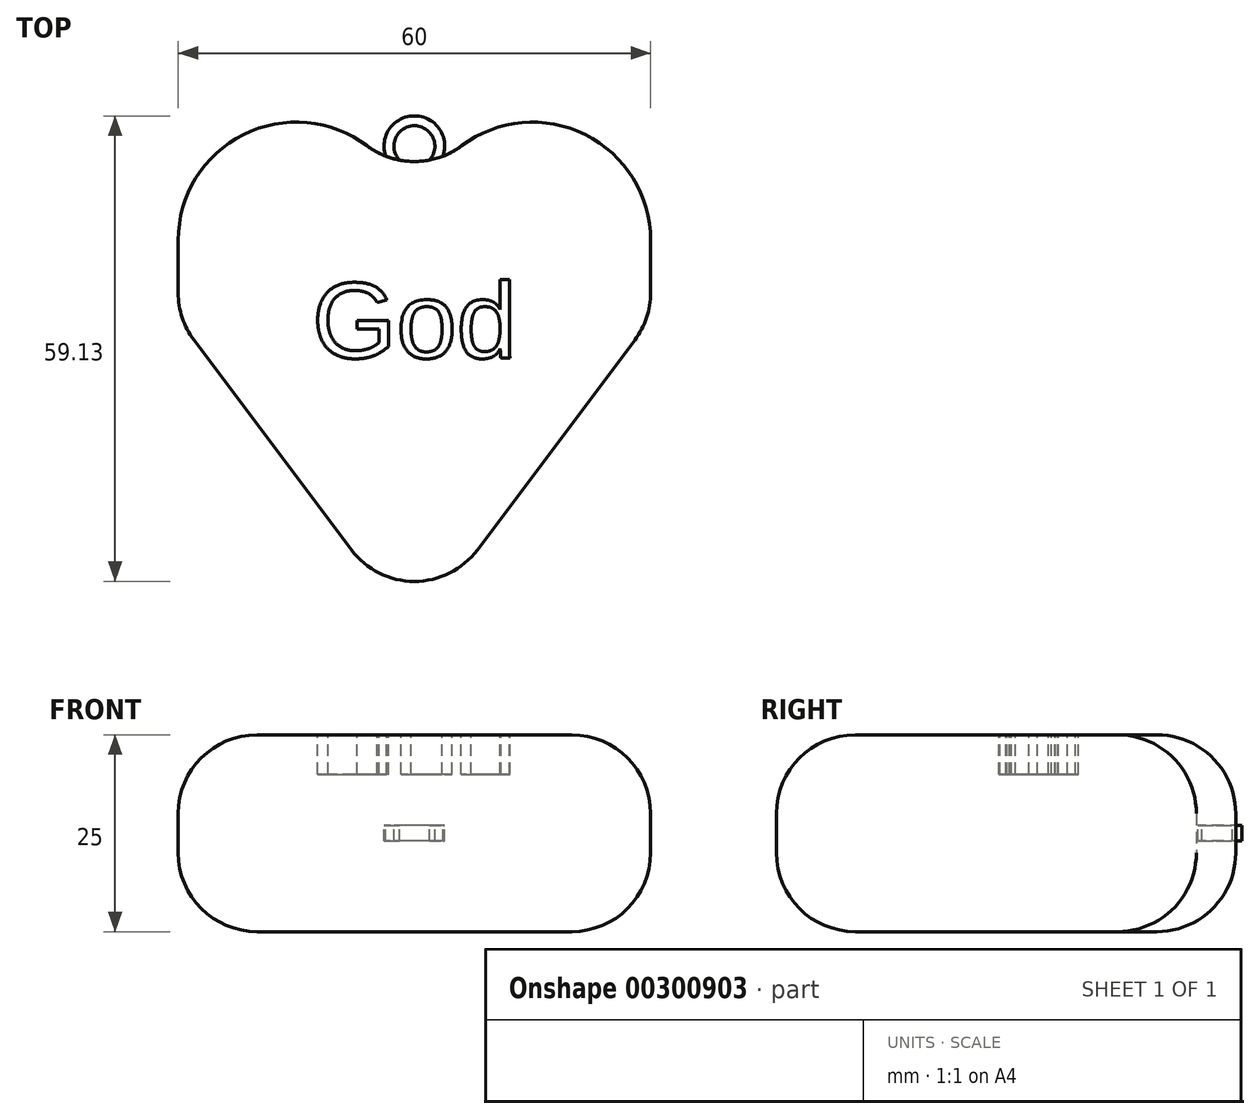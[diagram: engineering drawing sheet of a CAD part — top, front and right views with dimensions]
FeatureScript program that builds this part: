
annotation { "Feature Type Name" : "Feature", "Feature Type Description" : "" }
export const myFeature = defineFeature(function(context is Context, id is Id, definition is map)
    precondition{}
    {
        {
            var Q0;
            Q0=qCreatedBy(makeId("Top.planeOp"),FACE);
            var sketch = newSketch(context, id + "F0", { "sketchPlane" : qUnion([Q0])});
            skLineSegment(sketch, "E0", {"start": v(-30, 0) * mm, "end": v(0, -40) * mm});
            skLineSegment(sketch, "E1", {"start": v(-30, 10) * mm, "end": v(-30, 0) * mm});
            skLineSegment(sketch, "E2", {"start": v(0, 10) * mm, "end": v(0, 0) * mm});
            skArc(sketch, "E3", {"start": v(-30, 10) * mm, "mid": v(-15, 25) * mm, "end": v(0, 10) * mm});
            skArc(sketch, "E4.MirrorCS", {"start": v(30, 10) * mm, "mid": v(15, 25) * mm, "end": v(0, 10) * mm});
            skLineSegment(sketch, "E5.MirrorCS", {"start": v(30, 10) * mm, "end": v(30, 0) * mm});
            skLineSegment(sketch, "E6.MirrorCS", {"start": v(30, 0) * mm, "end": v(0, -40) * mm});
            skSolve(sketch);
        }
        {
            var Q0;
            Q0 = qSketchRegion(id + "F0", true);
            extrude(context, id + "F1", {"entities" : qUnion([Q0]), "endBound" : BoundingType.SYMMETRIC, "oppositeDirection" : true, "depth" : 25 * mm});
        }
        {
            var Q0;
            Q0=makeQuery(id+"F1.opExtrude","CAP_EDGE",EDGE,{"disambiguationData":[OSD([sQuery(id+"F0.wireOp",EDGE,"E5.MirrorCS")])],"isStart":false});
            var Q1;
            Q1=makeQuery(id+"F1.opExtrude","CAP_FACE",FACE,{"disambiguationData":[OSD([sQuery(id+"F0.wireOp",EDGE,"E0"),sQuery(id+"F0.wireOp",EDGE,"E1"),sQuery(id+"F0.wireOp",EDGE,"E3"),sQuery(id+"F0.wireOp",EDGE,"E4.MirrorCS"),sQuery(id+"F0.wireOp",EDGE,"E5.MirrorCS"),sQuery(id+"F0.wireOp",EDGE,"E6.MirrorCS")])],"isStart":false});
            var Q2;
            Q2=makeQuery(id+"F1.opExtrude","CAP_EDGE",EDGE,{"disambiguationData":[OSD([sQuery(id+"F0.wireOp",EDGE,"E4.MirrorCS")])],"isStart":false});
            var Q3;
            Q3=makeQuery(id+"F1.opExtrude","CAP_FACE",FACE,{"disambiguationData":[OSD([sQuery(id+"F0.wireOp",EDGE,"E0"),sQuery(id+"F0.wireOp",EDGE,"E1"),sQuery(id+"F0.wireOp",EDGE,"E3"),sQuery(id+"F0.wireOp",EDGE,"E4.MirrorCS"),sQuery(id+"F0.wireOp",EDGE,"E5.MirrorCS"),sQuery(id+"F0.wireOp",EDGE,"E6.MirrorCS")])],"isStart":true});
            var Q4;
            Q4=makeQuery(id+"F1.opExtrude","SWEPT_EDGE",EDGE,{"disambiguationData":[OSD([sQuery(id+"F0.wireOp",EDGE,"E4.MirrorCS"),sQuery(id+"F0.wireOp",EDGE,"E5.MirrorCS")])]});
            var Q5;
            Q5=makeQuery(id+"F1.opExtrude","SWEPT_EDGE",EDGE,{"disambiguationData":[OSD([sQuery(id+"F0.wireOp",EDGE,"E5.MirrorCS"),sQuery(id+"F0.wireOp",EDGE,"E6.MirrorCS")])]});
            var Q6;
            Q6=makeQuery(id+"F1.opExtrude","SWEPT_EDGE",EDGE,{"disambiguationData":[OSD([sQuery(id+"F0.wireOp",EDGE,"E0"),sQuery(id+"F0.wireOp",EDGE,"E6.MirrorCS")])]});
            var Q7;
            Q7=makeQuery(id+"F1.opExtrude","SWEPT_EDGE",EDGE,{"disambiguationData":[OSD([sQuery(id+"F0.wireOp",EDGE,"E1"),sQuery(id+"F0.wireOp",EDGE,"E3")])]});
            var Q8;
            Q8=makeQuery(id+"F1.opExtrude","SWEPT_EDGE",EDGE,{"disambiguationData":[OSD([sQuery(id+"F0.wireOp",EDGE,"E0"),sQuery(id+"F0.wireOp",EDGE,"E1")])]});
            var Q9;
            Q9=makeQuery(id+"F1.opExtrude","SWEPT_FACE",FACE,{"disambiguationData":[OSD([sQuery(id+"F0.wireOp",EDGE,"E4.MirrorCS")])]});
            fillet(context, id + "F2", {"entities" : qUnion([Q0, Q1, Q2, Q3, Q4, Q5, Q6, Q7, Q8, Q9]), "radius" : 10 * mm, "tangentPropagation" : true, "allowEdgeOverflow" : false});
        }
        {
            var Q0;
            Q0=qCreatedBy(makeId("Top.planeOp"),FACE);
            var sketch = newSketch(context, id + "F3", { "sketchPlane" : qUnion([Q0])});
            skCircle(sketch, "E7", {"center": v(0, 21.95) * mm, "radius": 3.85 * mm});
            skCircle(sketch, "E8.0", {"center": v(0, 21.95) * mm, "radius": 2.6 * mm});
            skSolve(sketch);
        }
        {
            var Q0;
            Q0=makeQuery(id+"F1.opExtrude","CAP_FACE",FACE,{"disambiguationData":[OSD([sQuery(id+"F0.wireOp",EDGE,"E0"),sQuery(id+"F0.wireOp",EDGE,"E1"),sQuery(id+"F0.wireOp",EDGE,"E3"),sQuery(id+"F0.wireOp",EDGE,"E4.MirrorCS"),sQuery(id+"F0.wireOp",EDGE,"E5.MirrorCS"),sQuery(id+"F0.wireOp",EDGE,"E6.MirrorCS")])],"isStart":true});
            var sketch = newSketch(context, id + "F4", { "sketchPlane" : qUnion([Q0])});
            skText(sketch, "E9", { "text": "God", "fontName": "Arimo-Regular.ttf"});
            const initialGuessF4  = {"E9": [-0.01297, -0.00494, 1, 0, 0.0099]};
            skSetInitialGuess(sketch, initialGuessF4);
            skSolve(sketch);
        }
        {
            var Q0;
            Q0=makeQuery(id+"F4.imprint","IMPRINT",FACE,{"disambiguationData":[TD([[makeQuery(id+"F4.imprint","IMPRINT",EDGE,{"derivedFrom":sQuery(id+"F4.wireOp",EDGE,"E9.sketch_text.stroke-38")}),-1.0]])]});
            var Q1;
            Q1=makeQuery(id+"F4.imprint","IMPRINT",FACE,{"disambiguationData":[TD([[makeQuery(id+"F4.imprint","IMPRINT",EDGE,{"derivedFrom":sQuery(id+"F4.wireOp",EDGE,"E9.sketch_text.stroke-0")}),-1.0]])]});
            var Q2;
            Q2=makeQuery(id+"F4.imprint","IMPRINT",FACE,{"disambiguationData":[TD([[makeQuery(id+"F4.imprint","IMPRINT",EDGE,{"derivedFrom":sQuery(id+"F4.wireOp",EDGE,"E9.sketch_text.stroke-23")}),-1.0]])]});
            extrude(context, id + "F5", {"entities" : qUnion([Q0, Q1, Q2]), "operationType" : NewBodyOperationType.REMOVE, "oppositeDirection" : true, "depth" : 5 * mm});
        }
        {
            var Q0;
            Q0=makeQuery(id+"F3.imprint","IMPRINT",FACE,{"disambiguationData":[TD([[makeQuery(id+"F3.imprint","IMPRINT",EDGE,{"derivedFrom":sQuery(id+"F3.wireOp",EDGE,"E7")}),1.0]])]});
            extrude(context, id + "F6", {"entities" : qUnion([Q0]), "operationType" : NewBodyOperationType.ADD, "endBound" : BoundingType.SYMMETRIC, "oppositeDirection" : true, "depth" : 2 * mm});
        }
    });
